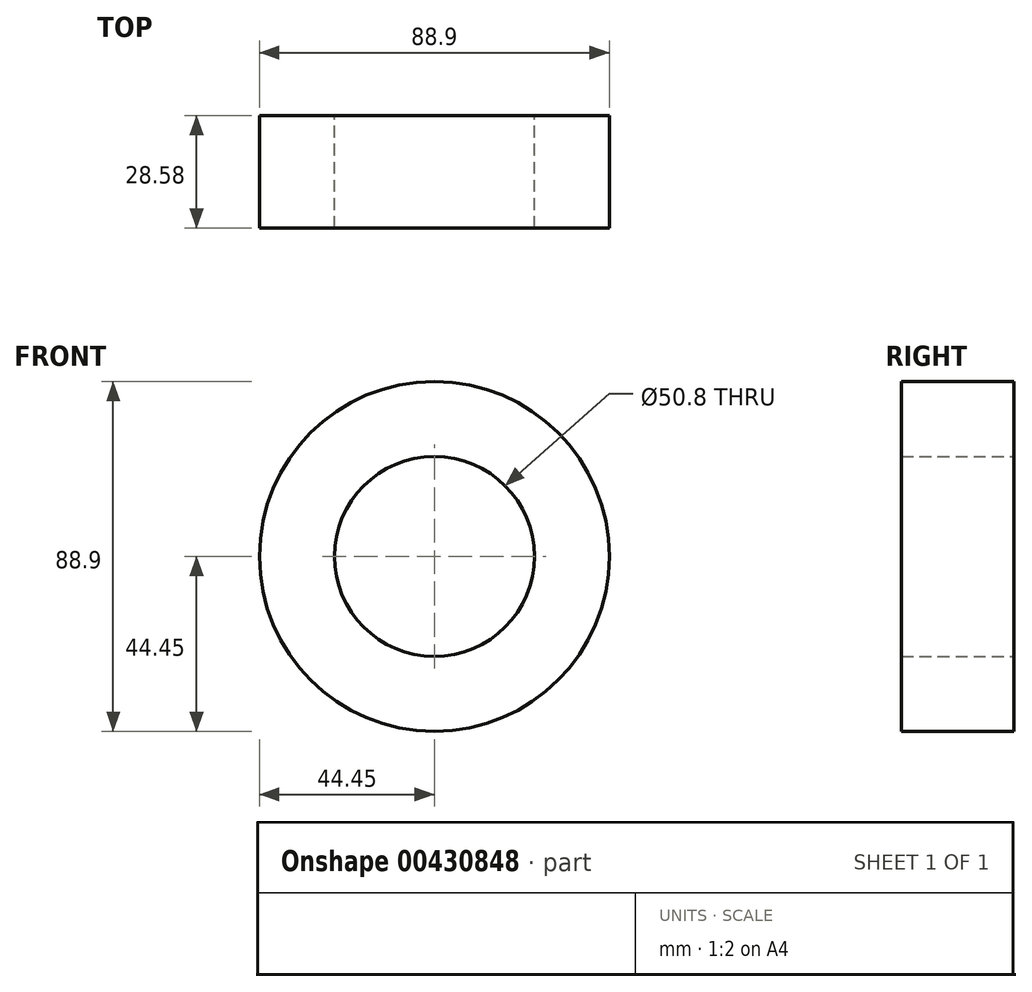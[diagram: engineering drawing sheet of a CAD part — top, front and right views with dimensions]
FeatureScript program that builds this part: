
annotation { "Feature Type Name" : "Feature", "Feature Type Description" : "" }
export const myFeature = defineFeature(function(context is Context, id is Id, definition is map)
    precondition{}
    {
        {
            var Q0;
            Q0=qCreatedBy(makeId("Front.planeOp"),FACE);
            var sketch = newSketch(context, id + "F0", { "sketchPlane" : qUnion([Q0])});
            skCircle(sketch, "E0", {"center": v(0, 0) * mm, "radius": 25.4 * mm});
            skCircle(sketch, "E1", {"center": v(0, 0) * mm, "radius": 44.45 * mm});
            skSolve(sketch);
        }
        {
            var Q0;
            Q0=sQuery(id+"F0.wireOp",EDGE,"E0");
            extrude(context, id + "F1", {"bodyType" : ToolBodyType.SURFACE, "surfaceEntities" : qUnion([Q0]), "depth" : 38.1 * mm});
        }
        {
            var Q0;
            Q0=makeQuery(id+"F0.imprint","IMPRINT",FACE,{"disambiguationData":[TD([[makeQuery(id+"F0.imprint","IMPRINT",EDGE,{"derivedFrom":sQuery(id+"F0.wireOp",EDGE,"E0")}),-1.0]])]});
            extrude(context, id + "F2", {"entities" : qUnion([Q0]), "depth" : 3.17 * mm});
        }
        {
            var Q0;
            Q0 = qSketchRegion(id + "F0", true);
            var Q1;
            Q1=makeQuery(id+"F2.opExtrude","CAP_FACE",FACE,{"disambiguationData":[OSD([sQuery(id+"F0.wireOp",EDGE,"E0"),sQuery(id+"F0.wireOp",EDGE,"E1")])],"isStart":false});
            extrude(context, id + "F3", {"entities" : qUnion([Q0, Q1]), "operationType" : NewBodyOperationType.ADD, "depth" : 25.4 * mm});
        }
    });
